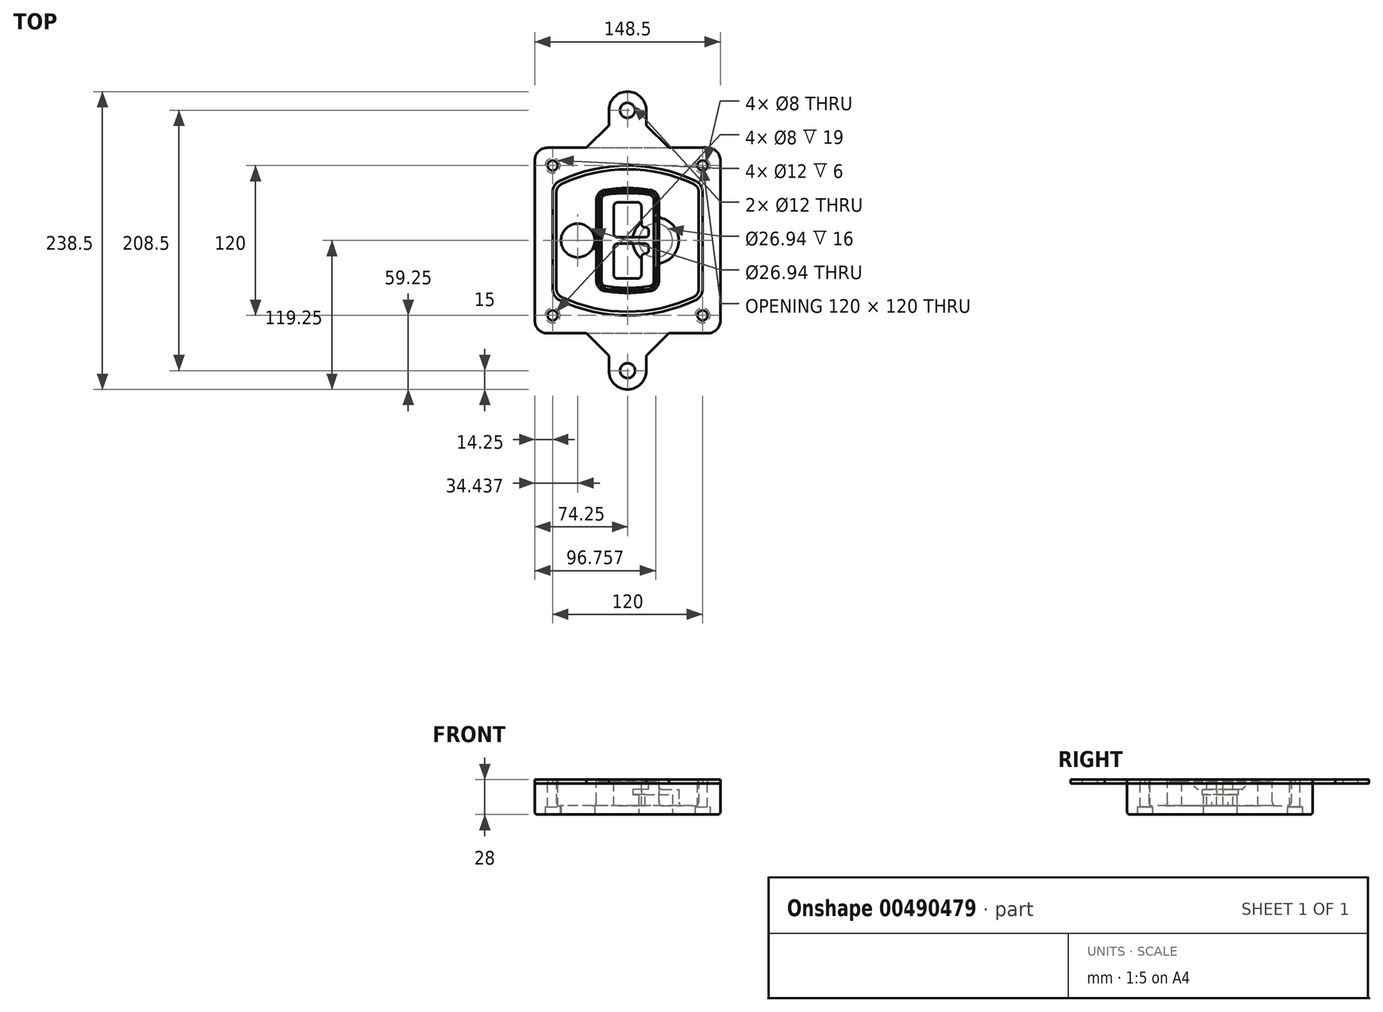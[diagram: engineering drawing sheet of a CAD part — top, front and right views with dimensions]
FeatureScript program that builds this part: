
annotation { "Feature Type Name" : "Feature", "Feature Type Description" : "" }
export const myFeature = defineFeature(function(context is Context, id is Id, definition is map)
    precondition{}
    {
        {
            var Q0;
            Q0=qCreatedBy(makeId("Top.planeOp"),FACE);
            var sketch = newSketch(context, id + "F0", { "sketchPlane" : qUnion([Q0])});
            skPoint(sketch, "E0.rect.middle", {"position": v(0, 0) * mm});
            skLineSegment(sketch, "E1.bottom", {"start": v(-64.25, -74.25) * mm, "end": v(64.25, -74.25) * mm});
            skLineSegment(sketch, "E1.top", {"start": v(-64.25, 74.25) * mm, "end": v(64.25, 74.25) * mm});
            skLineSegment(sketch, "E1.left", {"start": v(-74.25, -64.25) * mm, "end": v(-74.25, 64.25) * mm});
            skLineSegment(sketch, "E1.right", {"start": v(74.25, -64.25) * mm, "end": v(74.25, 64.25) * mm});
            skLineSegment(sketch, "E2", {"start": v(-74.25, 74.25) * mm, "end": v(74.25, -74.25) * mm, "construction": true});
            skLineSegment(sketch, "E3", {"start": v(74.25, 74.25) * mm, "end": v(-74.25, -74.25) * mm, "construction": true});
            skCircle(sketch, "E4", {"center": v(-60, 60) * mm, "radius": 4 * mm});
            skCircle(sketch, "E5", {"center": v(60, 60) * mm, "radius": 4 * mm});
            skCircle(sketch, "E6", {"center": v(60, -60) * mm, "radius": 4 * mm});
            skCircle(sketch, "E7", {"center": v(-60, -60) * mm, "radius": 4 * mm});
            skLineSegment(sketch, "E8", {"start": v(-60, 60) * mm, "end": v(60, 60) * mm, "construction": true});
            skLineSegment(sketch, "E9", {"start": v(60, 60) * mm, "end": v(60, -60) * mm, "construction": true});
            skLineSegment(sketch, "E10", {"start": v(60, -60) * mm, "end": v(-60, -60) * mm, "construction": true});
            skLineSegment(sketch, "E11", {"start": v(-60, -60) * mm, "end": v(-60, 60) * mm, "construction": true});
            skLineSegment(sketch, "E12", {"start": v(-60, 38.83) * mm, "end": v(-60, -38.83) * mm});
            skLineSegment(sketch, "E13", {"start": v(60, 38.83) * mm, "end": v(60, -38.83) * mm});
            skArc(sketch, "E14", {"start": v(54.26, 47.88) * mm, "mid": v(0, 60) * mm, "end": v(-54.26, 47.88) * mm});
            skArc(sketch, "E15", {"start": v(-54.26, -47.88) * mm, "mid": v(0, -60) * mm, "end": v(54.26, -47.88) * mm});
            skLineSegment(sketch, "E16", {"start": v(-60, 0) * mm, "end": v(60, 0) * mm, "construction": true});
            skPoint(sketch, "E17.visualSharp", {"position": v(-60, -45) * mm});
            skArc(sketch, "E17.filletArc", {"start": v(-60, -38.83) * mm, "mid": v(-58.44, -44.2) * mm, "end": v(-54.26, -47.88) * mm});
            skPoint(sketch, "E18.visualSharp", {"position": v(-60, 45) * mm});
            skArc(sketch, "E18.filletArc", {"start": v(-54.26, 47.88) * mm, "mid": v(-58.44, 44.2) * mm, "end": v(-60, 38.83) * mm});
            skPoint(sketch, "E19.visualSharp", {"position": v(60, 45) * mm});
            skArc(sketch, "E19.filletArc", {"start": v(60, 38.83) * mm, "mid": v(58.44, 44.2) * mm, "end": v(54.26, 47.88) * mm});
            skPoint(sketch, "E20.visualSharp", {"position": v(60, -45) * mm});
            skArc(sketch, "E20.filletArc", {"start": v(54.26, -47.88) * mm, "mid": v(58.44, -44.2) * mm, "end": v(60, -38.83) * mm});
            skPoint(sketch, "E21.visualSharp", {"position": v(-74.25, 74.25) * mm});
            skArc(sketch, "E21.filletArc", {"start": v(-64.25, 74.25) * mm, "mid": v(-71.32, 71.32) * mm, "end": v(-74.25, 64.25) * mm});
            skPoint(sketch, "E22.visualSharp", {"position": v(74.25, 74.25) * mm});
            skArc(sketch, "E22.filletArc", {"start": v(74.25, 64.25) * mm, "mid": v(71.32, 71.32) * mm, "end": v(64.25, 74.25) * mm});
            skPoint(sketch, "E23.visualSharp", {"position": v(74.25, -74.25) * mm});
            skArc(sketch, "E23.filletArc", {"start": v(64.25, -74.25) * mm, "mid": v(71.32, -71.32) * mm, "end": v(74.25, -64.25) * mm});
            skPoint(sketch, "E24.visualSharp", {"position": v(-74.25, -74.25) * mm});
            skArc(sketch, "E24.filletArc", {"start": v(-74.25, -64.25) * mm, "mid": v(-71.32, -71.32) * mm, "end": v(-64.25, -74.25) * mm});
            skArc(sketch, "E25.0", {"start": v(57, 38.83) * mm, "mid": v(55.9, 42.58) * mm, "end": v(52.98, 45.17) * mm});
            skLineSegment(sketch, "E25.1", {"start": v(57, 38.83) * mm, "end": v(57, -38.83) * mm});
            skArc(sketch, "E25.2", {"start": v(52.98, -45.17) * mm, "mid": v(55.9, -42.58) * mm, "end": v(57, -38.83) * mm});
            skArc(sketch, "E25.3", {"start": v(-52.98, -45.17) * mm, "mid": v(0, -57) * mm, "end": v(52.98, -45.17) * mm});
            skArc(sketch, "E25.4", {"start": v(-57, -38.83) * mm, "mid": v(-55.9, -42.58) * mm, "end": v(-52.98, -45.17) * mm});
            skArc(sketch, "E25.5", {"start": v(52.98, 45.17) * mm, "mid": v(0, 57) * mm, "end": v(-52.98, 45.17) * mm});
            skLineSegment(sketch, "E25.6", {"start": v(-57, 38.83) * mm, "end": v(-57, -38.83) * mm});
            skArc(sketch, "E25.7", {"start": v(-52.98, 45.17) * mm, "mid": v(-55.9, 42.58) * mm, "end": v(-57, 38.83) * mm});
            skArc(sketch, "E26.0", {"start": v(-55.96, 51.5) * mm, "mid": v(-61.82, 46.33) * mm, "end": v(-64, 38.83) * mm});
            skArc(sketch, "E26.1", {"start": v(55.96, 51.5) * mm, "mid": v(0, 64) * mm, "end": v(-55.96, 51.5) * mm});
            skArc(sketch, "E26.2", {"start": v(64, 38.83) * mm, "mid": v(61.82, 46.33) * mm, "end": v(55.96, 51.5) * mm});
            skLineSegment(sketch, "E26.3", {"start": v(64, 38.83) * mm, "end": v(64, -38.83) * mm});
            skArc(sketch, "E26.4", {"start": v(55.96, -51.5) * mm, "mid": v(61.82, -46.33) * mm, "end": v(64, -38.83) * mm});
            skLineSegment(sketch, "E26.5", {"start": v(-64, 38.83) * mm, "end": v(-64, -38.83) * mm});
            skArc(sketch, "E26.6", {"start": v(-55.96, -51.5) * mm, "mid": v(0, -64) * mm, "end": v(55.96, -51.5) * mm});
            skArc(sketch, "E26.7", {"start": v(-64, -38.83) * mm, "mid": v(-61.82, -46.33) * mm, "end": v(-55.96, -51.5) * mm});
            skSolve(sketch);
        }
        {
            var Q0;
            Q0=makeQuery(id+"F0.imprint","IMPRINT",FACE,{"disambiguationData":[TD([[makeQuery(id+"F0.imprint","IMPRINT",EDGE,{"derivedFrom":sQuery(id+"F0.wireOp",EDGE,"E1.bottom")}),1.0]])]});
            var Q1;
            Q1=makeQuery(id+"F0.imprint","IMPRINT",FACE,{"disambiguationData":[TD([[makeQuery(id+"F0.imprint","IMPRINT",EDGE,{"derivedFrom":sQuery(id+"F0.wireOp",EDGE,"E12")}),1.0]])]});
            var Q2;
            Q2=makeQuery(id+"F0.imprint","IMPRINT",FACE,{"disambiguationData":[TD([[makeQuery(id+"F0.imprint","IMPRINT",EDGE,{"derivedFrom":sQuery(id+"F0.wireOp",EDGE,"E25.0")}),1.0]])]});
            var Q3;
            Q3=makeQuery(id+"F0.imprint","IMPRINT",FACE,{"disambiguationData":[TD([[makeQuery(id+"F0.imprint","IMPRINT",EDGE,{"derivedFrom":sQuery(id+"F0.wireOp",EDGE,"E12")}),-1.0]])]});
            extrude(context, id + "F1", {"entities" : qUnion([Q0, Q1, Q2, Q3]), "oppositeDirection" : true, "depth" : 25 * mm});
        }
        {
            var Q0;
            Q0=makeQuery(id+"F0.imprint","IMPRINT",FACE,{"disambiguationData":[TD([[makeQuery(id+"F0.imprint","IMPRINT",EDGE,{"derivedFrom":sQuery(id+"F0.wireOp",EDGE,"E12")}),1.0]])]});
            extrude(context, id + "F2", {"entities" : qUnion([Q0]), "operationType" : NewBodyOperationType.ADD, "depth" : 3 * mm});
        }
        {
            var Q0;
            Q0=makeQuery(id+"F0.imprint","IMPRINT",FACE,{"disambiguationData":[TD([[makeQuery(id+"F0.imprint","IMPRINT",EDGE,{"derivedFrom":sQuery(id+"F0.wireOp",EDGE,"E25.0")}),1.0]])]});
            extrude(context, id + "F3", {"entities" : qUnion([Q0]), "operationType" : NewBodyOperationType.REMOVE, "oppositeDirection" : true, "depth" : 18 * mm});
        }
        {
            var Q0;
            Q0=makeQuery(id+"F2.opExtrude","CAP_FACE",FACE,{"disambiguationData":[OSD([sQuery(id+"F0.wireOp",EDGE,"E12"),sQuery(id+"F0.wireOp",EDGE,"E13"),sQuery(id+"F0.wireOp",EDGE,"E14"),sQuery(id+"F0.wireOp",EDGE,"E15"),sQuery(id+"F0.wireOp",EDGE,"E17.filletArc"),sQuery(id+"F0.wireOp",EDGE,"E18.filletArc"),sQuery(id+"F0.wireOp",EDGE,"E19.filletArc"),sQuery(id+"F0.wireOp",EDGE,"E20.filletArc"),sQuery(id+"F0.wireOp",EDGE,"E25.0"),sQuery(id+"F0.wireOp",EDGE,"E25.1"),sQuery(id+"F0.wireOp",EDGE,"E25.2"),sQuery(id+"F0.wireOp",EDGE,"E25.3"),sQuery(id+"F0.wireOp",EDGE,"E25.4"),sQuery(id+"F0.wireOp",EDGE,"E25.5"),sQuery(id+"F0.wireOp",EDGE,"E25.6"),sQuery(id+"F0.wireOp",EDGE,"E25.7")])],"isStart":false});
            var sketch = newSketch(context, id + "F4", { "sketchPlane" : qUnion([Q0])});
            skArc(sketch, "E27.0", {"start": v(-18.34, -40.45) * mm, "mid": v(0, -42) * mm, "end": v(18.34, -40.45) * mm});
            skArc(sketch, "E28.0", {"start": v(18.34, 40.45) * mm, "mid": v(0, 42) * mm, "end": v(-18.34, 40.45) * mm});
            skLineSegment(sketch, "E29", {"start": v(-25, 32.57) * mm, "end": v(-25, -32.57) * mm});
            skLineSegment(sketch, "E30", {"start": v(25, 32.57) * mm, "end": v(25, -32.57) * mm});
            skLineSegment(sketch, "E31", {"start": v(-25, 39.1) * mm, "end": v(25, 39.1) * mm, "construction": true});
            skLineSegment(sketch, "E32", {"start": v(-25, -39.1) * mm, "end": v(25, -39.1) * mm, "construction": true});
            skPoint(sketch, "E33.visualSharp", {"position": v(-25, 39.1) * mm});
            skArc(sketch, "E33.filletArc", {"start": v(-18.34, 40.45) * mm, "mid": v(-23.11, 37.73) * mm, "end": v(-25, 32.57) * mm});
            skPoint(sketch, "E34.visualSharp", {"position": v(25, 39.1) * mm});
            skArc(sketch, "E34.filletArc", {"start": v(25, 32.57) * mm, "mid": v(23.11, 37.73) * mm, "end": v(18.34, 40.45) * mm});
            skPoint(sketch, "E35.visualSharp", {"position": v(25, -39.1) * mm});
            skArc(sketch, "E35.filletArc", {"start": v(18.34, -40.45) * mm, "mid": v(23.11, -37.73) * mm, "end": v(25, -32.57) * mm});
            skPoint(sketch, "E36.visualSharp", {"position": v(-25, -39.1) * mm});
            skArc(sketch, "E36.filletArc", {"start": v(-25, -32.57) * mm, "mid": v(-23.11, -37.73) * mm, "end": v(-18.34, -40.45) * mm});
            skArc(sketch, "E37.0", {"start": v(52.98, 45.17) * mm, "mid": v(0, 57) * mm, "end": v(-52.98, 45.17) * mm});
            skArc(sketch, "E37.1", {"start": v(-52.98, 45.17) * mm, "mid": v(-55.9, 42.58) * mm, "end": v(-57, 38.83) * mm});
            skLineSegment(sketch, "E37.2", {"start": v(-57, 38.83) * mm, "end": v(-57, -38.83) * mm});
            skArc(sketch, "E37.3", {"start": v(-57, -38.83) * mm, "mid": v(-55.9, -42.58) * mm, "end": v(-52.98, -45.17) * mm});
            skArc(sketch, "E37.4", {"start": v(-52.98, -45.17) * mm, "mid": v(0, -57) * mm, "end": v(52.98, -45.17) * mm});
            skArc(sketch, "E37.5", {"start": v(52.98, -45.17) * mm, "mid": v(55.9, -42.58) * mm, "end": v(57, -38.83) * mm});
            skLineSegment(sketch, "E37.6", {"start": v(57, 38.83) * mm, "end": v(57, -38.83) * mm});
            skArc(sketch, "E37.7", {"start": v(57, 38.83) * mm, "mid": v(55.9, 42.58) * mm, "end": v(52.98, 45.17) * mm});
            skLineSegment(sketch, "E38.0", {"start": v(23, 32.57) * mm, "end": v(23, -32.57) * mm});
            skArc(sketch, "E38.1", {"start": v(18, -38.48) * mm, "mid": v(21.58, -36.44) * mm, "end": v(23, -32.57) * mm});
            skArc(sketch, "E38.2", {"start": v(-18, -38.48) * mm, "mid": v(0, -40) * mm, "end": v(18, -38.48) * mm});
            skArc(sketch, "E38.3", {"start": v(-23, -32.57) * mm, "mid": v(-21.58, -36.44) * mm, "end": v(-18, -38.48) * mm});
            skLineSegment(sketch, "E38.4", {"start": v(-23, 32.57) * mm, "end": v(-23, -32.57) * mm});
            skArc(sketch, "E38.5", {"start": v(23, 32.57) * mm, "mid": v(21.58, 36.44) * mm, "end": v(18, 38.48) * mm});
            skArc(sketch, "E38.6", {"start": v(-18, 38.48) * mm, "mid": v(-21.58, 36.44) * mm, "end": v(-23, 32.57) * mm});
            skArc(sketch, "E38.7", {"start": v(18, 38.48) * mm, "mid": v(0, 40) * mm, "end": v(-18, 38.48) * mm});
            skArc(sketch, "E39.0", {"start": v(21, 32.57) * mm, "mid": v(20.06, 35.15) * mm, "end": v(17.67, 36.5) * mm});
            skLineSegment(sketch, "E39.1", {"start": v(21, 32.57) * mm, "end": v(21, -32.57) * mm});
            skArc(sketch, "E39.2", {"start": v(17.67, -36.5) * mm, "mid": v(20.06, -35.15) * mm, "end": v(21, -32.57) * mm});
            skArc(sketch, "E39.3", {"start": v(-17.67, -36.5) * mm, "mid": v(0, -38) * mm, "end": v(17.67, -36.5) * mm});
            skArc(sketch, "E39.4", {"start": v(-21, -32.57) * mm, "mid": v(-20.06, -35.15) * mm, "end": v(-17.67, -36.5) * mm});
            skArc(sketch, "E39.5", {"start": v(17.67, 36.5) * mm, "mid": v(0, 38) * mm, "end": v(-17.67, 36.5) * mm});
            skLineSegment(sketch, "E39.6", {"start": v(-21, 32.57) * mm, "end": v(-21, -32.57) * mm});
            skArc(sketch, "E39.7", {"start": v(-17.67, 36.5) * mm, "mid": v(-20.06, 35.15) * mm, "end": v(-21, 32.57) * mm});
            skLineSegment(sketch, "E40", {"start": v(-25, 0) * mm, "end": v(25, 0) * mm, "construction": true});
            skLineSegment(sketch, "E41", {"start": v(-11, 5.5) * mm, "end": v(-11, 27.5) * mm});
            skLineSegment(sketch, "E42", {"start": v(-8, 30.5) * mm, "end": v(8, 30.5) * mm});
            skLineSegment(sketch, "E43", {"start": v(11, 27.5) * mm, "end": v(11, 13.5) * mm});
            skLineSegment(sketch, "E44", {"start": v(14, 10.5) * mm, "end": v(14, 10.5) * mm});
            skLineSegment(sketch, "E45", {"start": v(17, 7.5) * mm, "end": v(17, 5.5) * mm});
            skLineSegment(sketch, "E46", {"start": v(14, 2.5) * mm, "end": v(-8, 2.5) * mm});
            skPoint(sketch, "E47.visualSharp", {"position": v(-11, 30.5) * mm});
            skArc(sketch, "E47.filletArc", {"start": v(-8, 30.5) * mm, "mid": v(-10.12, 29.62) * mm, "end": v(-11, 27.5) * mm});
            skPoint(sketch, "E48.visualSharp", {"position": v(11, 30.5) * mm});
            skArc(sketch, "E48.filletArc", {"start": v(11, 27.5) * mm, "mid": v(10.12, 29.62) * mm, "end": v(8, 30.5) * mm});
            skPoint(sketch, "E49.visualSharp", {"position": v(11, 10.5) * mm});
            skArc(sketch, "E49.filletArc", {"start": v(11, 13.5) * mm, "mid": v(11.88, 11.38) * mm, "end": v(14, 10.5) * mm});
            skPoint(sketch, "E50.visualSharp", {"position": v(17, 10.5) * mm});
            skArc(sketch, "E50.filletArc", {"start": v(17, 7.5) * mm, "mid": v(16.12, 9.62) * mm, "end": v(14, 10.5) * mm});
            skPoint(sketch, "E51.visualSharp", {"position": v(17, 2.5) * mm});
            skArc(sketch, "E51.filletArc", {"start": v(14, 2.5) * mm, "mid": v(16.12, 3.38) * mm, "end": v(17, 5.5) * mm});
            skPoint(sketch, "E52.visualSharp", {"position": v(-11, 2.5) * mm});
            skArc(sketch, "E52.filletArc", {"start": v(-11, 5.5) * mm, "mid": v(-10.12, 3.38) * mm, "end": v(-8, 2.5) * mm});
            skLineSegment(sketch, "E53.0.MirrorCS", {"start": v(14, -2.5) * mm, "end": v(-8, -2.5) * mm});
            skArc(sketch, "E54.0.MirrorCS", {"start": v(-11, -5.5) * mm, "mid": v(-10.12, -3.38) * mm, "end": v(-8, -2.5) * mm});
            skLineSegment(sketch, "E55.0.MirrorCS", {"start": v(-11, -5.5) * mm, "end": v(-11, -27.5) * mm});
            skArc(sketch, "E56.0.MirrorCS", {"start": v(-8, -30.5) * mm, "mid": v(-10.12, -29.62) * mm, "end": v(-11, -27.5) * mm});
            skLineSegment(sketch, "E57.0.MirrorCS", {"start": v(-8, -30.5) * mm, "end": v(8, -30.5) * mm});
            skArc(sketch, "E58.0.MirrorCS", {"start": v(11, -27.5) * mm, "mid": v(10.12, -29.62) * mm, "end": v(8, -30.5) * mm});
            skLineSegment(sketch, "E59.0.MirrorCS", {"start": v(11, -27.5) * mm, "end": v(11, -13.5) * mm});
            skArc(sketch, "E60.0.MirrorCS", {"start": v(11, -13.5) * mm, "mid": v(11.88, -11.38) * mm, "end": v(14, -10.5) * mm});
            skArc(sketch, "E61.0.MirrorCS", {"start": v(17, -7.5) * mm, "mid": v(16.12, -9.62) * mm, "end": v(14, -10.5) * mm});
            skLineSegment(sketch, "E62.0.MirrorCS", {"start": v(17, -7.5) * mm, "end": v(17, -5.5) * mm});
            skArc(sketch, "E63.0.MirrorCS", {"start": v(14, -2.5) * mm, "mid": v(16.12, -3.38) * mm, "end": v(17, -5.5) * mm});
            skSolve(sketch);
        }
        {
            var Q0;
            Q0=makeQuery(id+"F4.imprint","IMPRINT",FACE,{"disambiguationData":[TD([[makeQuery(id+"F4.imprint","IMPRINT",EDGE,{"derivedFrom":sQuery(id+"F4.wireOp",EDGE,"E27.0")}),1.0]])]});
            var Q1;
            Q1=makeQuery(id+"F4.imprint","IMPRINT",FACE,{"disambiguationData":[TD([[makeQuery(id+"F4.imprint","IMPRINT",EDGE,{"derivedFrom":sQuery(id+"F4.wireOp",EDGE,"E38.0")}),-1.0]])]});
            var Q2;
            Q2=makeQuery(id+"F4.imprint","IMPRINT",FACE,{"disambiguationData":[TD([[makeQuery(id+"F4.imprint","IMPRINT",EDGE,{"derivedFrom":sQuery(id+"F4.wireOp",EDGE,"E39.0")}),1.0]])]});
            extrude(context, id + "F5", {"entities" : qUnion([Q0, Q1, Q2]), "operationType" : NewBodyOperationType.ADD, "endBound" : BoundingType.UP_TO_NEXT, "oppositeDirection" : true, "depth" : 25 * mm});
        }
        {
            var Q0;
            Q0=makeQuery(id+"F4.imprint","IMPRINT",FACE,{"disambiguationData":[TD([[makeQuery(id+"F4.imprint","IMPRINT",EDGE,{"derivedFrom":sQuery(id+"F4.wireOp",EDGE,"E38.0")}),-1.0]])]});
            extrude(context, id + "F6", {"entities" : qUnion([Q0]), "operationType" : NewBodyOperationType.REMOVE, "oppositeDirection" : true, "depth" : 2 * mm});
        }
        {
            var Q0;
            Q0=makeQuery(id+"F1.opExtrude","CAP_FACE",FACE,{"disambiguationData":[OSD([sQuery(id+"F0.wireOp",EDGE,"E1.bottom"),sQuery(id+"F0.wireOp",EDGE,"E1.top"),sQuery(id+"F0.wireOp",EDGE,"E1.left"),sQuery(id+"F0.wireOp",EDGE,"E1.right"),sQuery(id+"F0.wireOp",EDGE,"E4"),sQuery(id+"F0.wireOp",EDGE,"E5"),sQuery(id+"F0.wireOp",EDGE,"E6"),sQuery(id+"F0.wireOp",EDGE,"E7"),sQuery(id+"F0.wireOp",EDGE,"E21.filletArc"),sQuery(id+"F0.wireOp",EDGE,"E22.filletArc"),sQuery(id+"F0.wireOp",EDGE,"E23.filletArc"),sQuery(id+"F0.wireOp",EDGE,"E24.filletArc")])],"isStart":false});
            var sketch = newSketch(context, id + "F7", { "sketchPlane" : qUnion([Q0])});
            skCircle(sketch, "E64", {"center": v(22.5, 0) * mm, "radius": 13.47 * mm});
            skCircle(sketch, "E65", {"center": v(-39.81, 0) * mm, "radius": 13.47 * mm});
            skLineSegment(sketch, "E66", {"start": v(74.25, 0) * mm, "end": v(-74.25, 0) * mm});
            skCircle(sketch, "E67", {"center": v(22.5, 0) * mm, "radius": 18.47 * mm});
            skCircle(sketch, "E68", {"center": v(60, -60) * mm, "radius": 6 * mm});
            skCircle(sketch, "E69", {"center": v(-60, -60) * mm, "radius": 6 * mm});
            skCircle(sketch, "E70", {"center": v(-60, 60) * mm, "radius": 6 * mm});
            skCircle(sketch, "E71", {"center": v(60, 60) * mm, "radius": 6 * mm});
            skSolve(sketch);
        }
        {
            var Q0;
            {var subQ1=sQuery(id+"F7.wireOp",EDGE,"E66");var subQ4=sQuery(id+"F7.wireOp",EDGE,"E64");var subQ6=makeQuery(id+"F7.imprint","INTERSECT",VERTEX,{"disambiguationData":[OD(0.0)],"derivedFrom":[subQ4,subQ1]});Q0=makeQuery(id+"F7.imprint","IMPRINT",FACE,{"disambiguationData":[TD([[makeQuery(id+"F7.imprint","IMPRINT",EDGE,{"disambiguationData":[TD([[subQ6,-1.0]])],"derivedFrom":subQ4}),-1.0]])]});}
            var Q1;
            {var subQ0=sQuery(id+"F7.wireOp",EDGE,"E66");var subQ1=sQuery(id+"F7.wireOp",EDGE,"E64");var subQ3=makeQuery(id+"F7.imprint","INTERSECT",VERTEX,{"disambiguationData":[OD(0.0)],"derivedFrom":[subQ1,subQ0]});Q1=makeQuery(id+"F7.imprint","IMPRINT",FACE,{"disambiguationData":[TD([[makeQuery(id+"F7.imprint","IMPRINT",EDGE,{"disambiguationData":[TD([[subQ3,-1.0]])],"derivedFrom":subQ1}),1.0]])]});}
            var Q2;
            {var subQ0=sQuery(id+"F7.wireOp",EDGE,"E66");var subQ1=sQuery(id+"F7.wireOp",EDGE,"E64");var subQ3=makeQuery(id+"F7.imprint","INTERSECT",VERTEX,{"disambiguationData":[OD(0.0)],"derivedFrom":[subQ1,subQ0]});Q2=makeQuery(id+"F7.imprint","IMPRINT",FACE,{"disambiguationData":[TD([[makeQuery(id+"F7.imprint","IMPRINT",EDGE,{"disambiguationData":[TD([[subQ3,1.0]])],"derivedFrom":subQ1}),1.0]])]});}
            var Q3;
            {var subQ1=sQuery(id+"F7.wireOp",EDGE,"E66");var subQ4=sQuery(id+"F7.wireOp",EDGE,"E64");var subQ6=makeQuery(id+"F7.imprint","INTERSECT",VERTEX,{"disambiguationData":[OD(0.0)],"derivedFrom":[subQ4,subQ1]});Q3=makeQuery(id+"F7.imprint","IMPRINT",FACE,{"disambiguationData":[TD([[makeQuery(id+"F7.imprint","IMPRINT",EDGE,{"disambiguationData":[TD([[subQ6,1.0]])],"derivedFrom":subQ4}),-1.0]])]});}
            extrude(context, id + "F8", {"entities" : qUnion([Q0, Q1, Q2, Q3]), "operationType" : NewBodyOperationType.ADD, "oppositeDirection" : true, "depth" : 20 * mm});
        }
        {
            var Q0;
            {var subQ0=sQuery(id+"F7.wireOp",EDGE,"E66");var subQ1=sQuery(id+"F7.wireOp",EDGE,"E64");var subQ3=makeQuery(id+"F7.imprint","INTERSECT",VERTEX,{"disambiguationData":[OD(0.0)],"derivedFrom":[subQ1,subQ0]});Q0=makeQuery(id+"F7.imprint","IMPRINT",FACE,{"disambiguationData":[TD([[makeQuery(id+"F7.imprint","IMPRINT",EDGE,{"disambiguationData":[TD([[subQ3,-1.0]])],"derivedFrom":subQ1}),1.0]])]});}
            var Q1;
            {var subQ0=sQuery(id+"F7.wireOp",EDGE,"E66");var subQ1=sQuery(id+"F7.wireOp",EDGE,"E64");var subQ3=makeQuery(id+"F7.imprint","INTERSECT",VERTEX,{"disambiguationData":[OD(0.0)],"derivedFrom":[subQ1,subQ0]});Q1=makeQuery(id+"F7.imprint","IMPRINT",FACE,{"disambiguationData":[TD([[makeQuery(id+"F7.imprint","IMPRINT",EDGE,{"disambiguationData":[TD([[subQ3,1.0]])],"derivedFrom":subQ1}),1.0]])]});}
            extrude(context, id + "F9", {"entities" : qUnion([Q0, Q1]), "operationType" : NewBodyOperationType.REMOVE, "oppositeDirection" : true, "depth" : 16 * mm});
        }
        {
            var Q0;
            {var subQ0=sQuery(id+"F7.wireOp",EDGE,"E66");var subQ1=sQuery(id+"F7.wireOp",EDGE,"E65");var subQ3=makeQuery(id+"F7.imprint","INTERSECT",VERTEX,{"disambiguationData":[OD(0.0)],"derivedFrom":[subQ1,subQ0]});Q0=makeQuery(id+"F7.imprint","IMPRINT",FACE,{"disambiguationData":[TD([[makeQuery(id+"F7.imprint","IMPRINT",EDGE,{"disambiguationData":[TD([[subQ3,-1.0]])],"derivedFrom":subQ1}),1.0]])]});}
            var Q1;
            {var subQ0=sQuery(id+"F7.wireOp",EDGE,"E66");var subQ1=sQuery(id+"F7.wireOp",EDGE,"E65");var subQ3=makeQuery(id+"F7.imprint","INTERSECT",VERTEX,{"disambiguationData":[OD(0.0)],"derivedFrom":[subQ1,subQ0]});Q1=makeQuery(id+"F7.imprint","IMPRINT",FACE,{"disambiguationData":[TD([[makeQuery(id+"F7.imprint","IMPRINT",EDGE,{"disambiguationData":[TD([[subQ3,1.0]])],"derivedFrom":subQ1}),1.0]])]});}
            extrude(context, id + "F10", {"entities" : qUnion([Q0, Q1]), "operationType" : NewBodyOperationType.REMOVE, "oppositeDirection" : true, "depth" : 25 * mm});
        }
        {
            var Q0;
            Q0=makeQuery(id+"F7.imprint","IMPRINT",FACE,{"disambiguationData":[TD([[makeQuery(id+"F7.imprint","IMPRINT",EDGE,{"derivedFrom":sQuery(id+"F7.wireOp",EDGE,"E68")}),1.0]])]});
            var Q1;
            Q1=makeQuery(id+"F7.imprint","IMPRINT",FACE,{"disambiguationData":[TD([[makeQuery(id+"F7.imprint","IMPRINT",EDGE,{"derivedFrom":makeQuery(id+"F1.opExtrude","CAP_EDGE",EDGE,{"disambiguationData":[OSD([sQuery(id+"F0.wireOp",EDGE,"E5")])],"isStart":false})}),-1.0]])]});
            var Q2;
            Q2=makeQuery(id+"F7.imprint","IMPRINT",FACE,{"disambiguationData":[TD([[makeQuery(id+"F7.imprint","IMPRINT",EDGE,{"derivedFrom":sQuery(id+"F7.wireOp",EDGE,"E69")}),1.0]])]});
            var Q3;
            Q3=makeQuery(id+"F7.imprint","IMPRINT",FACE,{"disambiguationData":[TD([[makeQuery(id+"F7.imprint","IMPRINT",EDGE,{"derivedFrom":makeQuery(id+"F1.opExtrude","CAP_EDGE",EDGE,{"disambiguationData":[OSD([sQuery(id+"F0.wireOp",EDGE,"E4")])],"isStart":false})}),-1.0]])]});
            var Q4;
            Q4=makeQuery(id+"F7.imprint","IMPRINT",FACE,{"disambiguationData":[TD([[makeQuery(id+"F7.imprint","IMPRINT",EDGE,{"derivedFrom":sQuery(id+"F7.wireOp",EDGE,"E70")}),1.0]])]});
            var Q5;
            Q5=makeQuery(id+"F7.imprint","IMPRINT",FACE,{"disambiguationData":[TD([[makeQuery(id+"F7.imprint","IMPRINT",EDGE,{"derivedFrom":makeQuery(id+"F1.opExtrude","CAP_EDGE",EDGE,{"disambiguationData":[OSD([sQuery(id+"F0.wireOp",EDGE,"E7")])],"isStart":false})}),-1.0]])]});
            var Q6;
            Q6=makeQuery(id+"F7.imprint","IMPRINT",FACE,{"disambiguationData":[TD([[makeQuery(id+"F7.imprint","IMPRINT",EDGE,{"derivedFrom":sQuery(id+"F7.wireOp",EDGE,"E71")}),1.0]])]});
            var Q7;
            Q7=makeQuery(id+"F7.imprint","IMPRINT",FACE,{"disambiguationData":[TD([[makeQuery(id+"F7.imprint","IMPRINT",EDGE,{"derivedFrom":makeQuery(id+"F1.opExtrude","CAP_EDGE",EDGE,{"disambiguationData":[OSD([sQuery(id+"F0.wireOp",EDGE,"E6")])],"isStart":false})}),-1.0]])]});
            extrude(context, id + "F11", {"entities" : qUnion([Q0, Q1, Q2, Q3, Q4, Q5, Q6, Q7]), "operationType" : NewBodyOperationType.REMOVE, "oppositeDirection" : true, "depth" : 6 * mm});
        }
        {
            var Q0;
            Q0=makeQuery(id+"F9.boolean.opBoolean","COPY",FACE,{"derivedFrom":makeQuery(id+"F9.opExtrude","CAP_FACE",FACE,{"disambiguationData":[OSD([sQuery(id+"F7.wireOp",EDGE,"E64")])],"isStart":false})});
            var sketch = newSketch(context, id + "F12", { "sketchPlane" : qUnion([Q0])});
            skArc(sketch, "E72.0", {"start": v(11, 14.45) * mm, "mid": v(6.45, 9.13) * mm, "end": v(4.2, 2.5) * mm});
            skArc(sketch, "E72.1", {"start": v(4.2, -2.5) * mm, "mid": v(6.45, -9.13) * mm, "end": v(11, -14.45) * mm});
            skLineSegment(sketch, "E73", {"start": v(4.2, -2.5) * mm, "end": v(14, -2.5) * mm});
            skLineSegment(sketch, "E74.0", {"start": v(14, 2.5) * mm, "end": v(4.2, 2.5) * mm});
            skArc(sketch, "E74.1", {"start": v(14, 2.5) * mm, "mid": v(16.12, 3.38) * mm, "end": v(17, 5.5) * mm});
            skLineSegment(sketch, "E74.2", {"start": v(17, 7.5) * mm, "end": v(17, 5.5) * mm});
            skArc(sketch, "E74.3", {"start": v(17, 7.5) * mm, "mid": v(16.12, 9.62) * mm, "end": v(14, 10.5) * mm});
            skArc(sketch, "E74.4", {"start": v(11, 13.5) * mm, "mid": v(11.88, 11.38) * mm, "end": v(14, 10.5) * mm});
            skLineSegment(sketch, "E74.5", {"start": v(11, 14.45) * mm, "end": v(11, 13.5) * mm});
            skLineSegment(sketch, "E74.7", {"start": v(14, -2.5) * mm, "end": v(4.2, -2.5) * mm});
            skArc(sketch, "E74.8", {"start": v(14, -2.5) * mm, "mid": v(16.12, -3.38) * mm, "end": v(17, -5.5) * mm});
            skLineSegment(sketch, "E74.9", {"start": v(17, -7.5) * mm, "end": v(17, -5.5) * mm});
            skArc(sketch, "E74.10", {"start": v(17, -7.5) * mm, "mid": v(16.12, -9.62) * mm, "end": v(14, -10.5) * mm});
            skArc(sketch, "E74.11", {"start": v(11, -13.5) * mm, "mid": v(11.88, -11.38) * mm, "end": v(14, -10.5) * mm});
            skLineSegment(sketch, "E74.12", {"start": v(11, -14.45) * mm, "end": v(11, -13.5) * mm});
            skPoint(sketch, "E75.orphan", {"position": v(11, -27.5) * mm});
            skPoint(sketch, "E76.orphan", {"position": v(-8, -2.5) * mm});
            skPoint(sketch, "E77.orphan", {"position": v(-8, 2.5) * mm});
            skPoint(sketch, "E78.orphan", {"position": v(11, 27.5) * mm});
            skSolve(sketch);
        }
        {
            var Q0;
            {var subQ7=sQuery(id+"F12.wireOp",EDGE,"E72.0");var subQ14=sQuery(id+"F12.wireOp",EDGE,"E72.1");var subQ16=sQuery(id+"F12.wireOp",EDGE,"E74.1");var subQ18=sQuery(id+"F12.wireOp",EDGE,"E74.8");Q0=qUnion([makeQuery(id+"F12.imprint","IMPRINT",FACE,{"disambiguationData":[TD([[makeQuery(id+"F12.imprint","IMPRINT",EDGE,{"derivedFrom":subQ7}),1.0]])]}),makeQuery(id+"F12.imprint","IMPRINT",FACE,{"disambiguationData":[TD([[makeQuery(id+"F12.imprint","IMPRINT",EDGE,{"derivedFrom":subQ14}),1.0]])]}),makeQuery(id+"F12.imprint","IMPRINT",FACE,{"disambiguationData":[TD([[makeQuery(id+"F12.imprint","IMPRINT",EDGE,{"derivedFrom":subQ16}),1.0]])]}),makeQuery(id+"F12.imprint","IMPRINT",FACE,{"disambiguationData":[TD([[makeQuery(id+"F12.imprint","IMPRINT",EDGE,{"derivedFrom":subQ18}),-1.0]])]})]);}
            var Q1;
            Q1=makeQuery(id+"F5.boolean.opBoolean","SPLIT",FACE,{"disambiguationData":[TD([makeQuery(id+"F5.opExtrude","SWEPT_FACE",FACE,{"disambiguationData":[OSD([sQuery(id+"F4.wireOp",EDGE,"E41")])]})])],"derivedFrom":makeQuery(id+"F3.boolean.opBoolean","COPY",FACE,{"derivedFrom":makeQuery(id+"F3.opExtrude","CAP_FACE",FACE,{"disambiguationData":[OSD([sQuery(id+"F0.wireOp",EDGE,"E25.0"),sQuery(id+"F0.wireOp",EDGE,"E25.1"),sQuery(id+"F0.wireOp",EDGE,"E25.2"),sQuery(id+"F0.wireOp",EDGE,"E25.3"),sQuery(id+"F0.wireOp",EDGE,"E25.4"),sQuery(id+"F0.wireOp",EDGE,"E25.5"),sQuery(id+"F0.wireOp",EDGE,"E25.6"),sQuery(id+"F0.wireOp",EDGE,"E25.7")])],"isStart":false})})});
            extrude(context, id + "F13", {"entities" : qUnion([Q0]), "operationType" : NewBodyOperationType.REMOVE, "endBound" : BoundingType.UP_TO_SURFACE, "endBoundEntityFace" : qUnion([Q1]), "depth" : 25 * mm});
        }
        {
            var Q0;
            Q0=makeQuery(id+"F3.boolean.opBoolean","COPY",EDGE,{"derivedFrom":makeQuery(id+"F3.opExtrude","CAP_EDGE",EDGE,{"disambiguationData":[OSD([sQuery(id+"F0.wireOp",EDGE,"E25.6")])],"isStart":false})});
            var Q1;
            Q1=makeQuery(id+"F8.boolean.opBoolean","INTERSECT",EDGE,{"derivedFrom":[makeQuery(id+"F5.opExtrude","SWEPT_FACE",FACE,{"disambiguationData":[OSD([sQuery(id+"F4.wireOp",EDGE,"E30")])]}),makeQuery(id+"F8.opExtrude","CAP_FACE",FACE,{"disambiguationData":[OSD([sQuery(id+"F7.wireOp",EDGE,"E67")])],"isStart":false})]});
            var Q2;
            Q2=makeQuery(id+"F8.boolean.opBoolean","INTERSECT",EDGE,{"disambiguationData":[OD(1.0)],"derivedFrom":[makeQuery(id+"F5.opExtrude","SWEPT_FACE",FACE,{"disambiguationData":[OSD([sQuery(id+"F4.wireOp",EDGE,"E30")])]}),makeQuery(id+"F8.opExtrude","SWEPT_FACE",FACE,{"disambiguationData":[OSD([sQuery(id+"F7.wireOp",EDGE,"E67")])]})]});
            var Q3;
            {var subQ0=sQuery(id+"F4.wireOp",EDGE,"E30");Q3=makeQuery(id+"F8.boolean.opBoolean","SPLIT",EDGE,{"disambiguationData":[TD([makeQuery(id+"F5.opExtrude","SWEPT_FACE",FACE,{"disambiguationData":[OSD([sQuery(id+"F4.wireOp",EDGE,"E35.filletArc")])]})])],"derivedFrom":makeQuery(id+"F5.opExtrude","CAP_EDGE",EDGE,{"disambiguationData":[OSD([subQ0])],"isStart":false})});}
            var Q4;
            {var subQ0=sQuery(id+"F0.wireOp",EDGE,"E25.7");var subQ1=sQuery(id+"F0.wireOp",EDGE,"E25.1");var subQ2=sQuery(id+"F0.wireOp",EDGE,"E25.6");var subQ3=sQuery(id+"F0.wireOp",EDGE,"E25.5");var subQ4=sQuery(id+"F0.wireOp",EDGE,"E25.4");var subQ5=sQuery(id+"F0.wireOp",EDGE,"E25.0");var subQ6=sQuery(id+"F0.wireOp",EDGE,"E25.2");var subQ7=sQuery(id+"F0.wireOp",EDGE,"E25.3");Q4=makeQuery(id+"F8.boolean.opBoolean","INTERSECT",EDGE,{"derivedFrom":[makeQuery(id+"F5.boolean.opBoolean","SPLIT",FACE,{"disambiguationData":[TD([makeQuery(id+"F2.opExtrude","SWEPT_FACE",FACE,{"disambiguationData":[OSD([subQ5])]})])],"derivedFrom":makeQuery(id+"F3.boolean.opBoolean","COPY",FACE,{"derivedFrom":makeQuery(id+"F3.opExtrude","CAP_FACE",FACE,{"disambiguationData":[OSD([subQ5,subQ1,subQ6,subQ7,subQ4,subQ3,subQ2,subQ0])],"isStart":false})})}),makeQuery(id+"F8.opExtrude","SWEPT_FACE",FACE,{"disambiguationData":[OSD([sQuery(id+"F7.wireOp",EDGE,"E67")])]})]});}
            var Q5;
            Q5=makeQuery(id+"F8.boolean.opBoolean","INTERSECT",EDGE,{"disambiguationData":[OD(0.0)],"derivedFrom":[makeQuery(id+"F5.opExtrude","SWEPT_FACE",FACE,{"disambiguationData":[OSD([sQuery(id+"F4.wireOp",EDGE,"E30")])]}),makeQuery(id+"F8.opExtrude","SWEPT_FACE",FACE,{"disambiguationData":[OSD([sQuery(id+"F7.wireOp",EDGE,"E67")])]})]});
            fillet(context, id + "F14", {"entities" : qUnion([Q0, Q1, Q2, Q3, Q4, Q5]), "radius" : 3 * mm, "tangentPropagation" : true, "allowEdgeOverflow" : false});
        }
        {
            var Q0;
            Q0=makeQuery(id+"F1.opExtrude","CAP_EDGE",EDGE,{"disambiguationData":[OSD([sQuery(id+"F0.wireOp",EDGE,"E1.bottom")])],"isStart":false});
            fillet(context, id + "F15", {"entities" : qUnion([Q0]), "radius" : 2 * mm, "tangentPropagation" : true, "allowEdgeOverflow" : false});
        }
        {
            var Q0;
            {var subQ0=sQuery(id+"F0.wireOp",EDGE,"E21.filletArc");var subQ1=sQuery(id+"F0.wireOp",EDGE,"E7");var subQ2=sQuery(id+"F0.wireOp",EDGE,"E6");var subQ3=sQuery(id+"F0.wireOp",EDGE,"E5");var subQ4=sQuery(id+"F0.wireOp",EDGE,"E4");var subQ5=sQuery(id+"F0.wireOp",EDGE,"E22.filletArc");var subQ6=sQuery(id+"F0.wireOp",EDGE,"E1.bottom");var subQ7=sQuery(id+"F0.wireOp",EDGE,"E1.right");var subQ8=sQuery(id+"F0.wireOp",EDGE,"E1.top");var subQ9=sQuery(id+"F0.wireOp",EDGE,"E1.left");var subQ10=sQuery(id+"F0.wireOp",EDGE,"E23.filletArc");var subQ11=sQuery(id+"F0.wireOp",EDGE,"E24.filletArc");Q0=makeQuery(id+"F2.boolean.opBoolean","SPLIT",FACE,{"disambiguationData":[TD([makeQuery(id+"F1.opExtrude","SWEPT_FACE",FACE,{"disambiguationData":[OSD([subQ6])]})])],"derivedFrom":makeQuery(id+"F1.opExtrude","CAP_FACE",FACE,{"disambiguationData":[OSD([subQ6,subQ8,subQ9,subQ7,subQ4,subQ3,subQ2,subQ1,subQ0,subQ5,subQ10,subQ11])],"isStart":true})});}
            var sketch = newSketch(context, id + "F16", { "sketchPlane" : qUnion([Q0])});
            skLineSegment(sketch, "E79", {"start": v(0, 74.25) * mm, "end": v(0, 104.25) * mm, "construction": true});
            skArc(sketch, "E80", {"start": v(15, 104.25) * mm, "mid": v(0, 119.25) * mm, "end": v(-15, 104.25) * mm});
            skLineSegment(sketch, "E81", {"start": v(15, 104.25) * mm, "end": v(15, 92.25) * mm});
            skLineSegment(sketch, "E82", {"start": v(-15, 104.25) * mm, "end": v(-15, 92.25) * mm});
            skLineSegment(sketch, "E83", {"start": v(-15, 92.25) * mm, "end": v(-33, 74.25) * mm});
            skLineSegment(sketch, "E84", {"start": v(15, 92.25) * mm, "end": v(33, 74.25) * mm});
            skCircle(sketch, "E85", {"center": v(0, 104.25) * mm, "radius": 6 * mm});
            skLineSegment(sketch, "E86", {"start": v(-74.25, 0) * mm, "end": v(74.25, 0) * mm, "construction": true});
            skLineSegment(sketch, "E87.MirrorCS", {"start": v(15, -104.25) * mm, "end": v(15, -92.25) * mm});
            skLineSegment(sketch, "E88.MirrorCS", {"start": v(-15, -104.25) * mm, "end": v(-15, -92.25) * mm});
            skCircle(sketch, "E89.MirrorC", {"center": v(0, -104.25) * mm, "radius": 6 * mm});
            skLineSegment(sketch, "E90.MirrorCS", {"start": v(0, -74.25) * mm, "end": v(0, -104.25) * mm, "construction": true});
            skArc(sketch, "E91.MirrorCS", {"start": v(15, -104.25) * mm, "mid": v(0, -119.25) * mm, "end": v(-15, -104.25) * mm});
            skLineSegment(sketch, "E92.MirrorCS", {"start": v(-15, -92.25) * mm, "end": v(-33, -74.25) * mm});
            skLineSegment(sketch, "E93.MirrorCS", {"start": v(15, -92.25) * mm, "end": v(33, -74.25) * mm});
            skSolve(sketch);
        }
        {
            var Q0;
            Q0=makeQuery(id+"F16.imprint","IMPRINT",FACE,{"disambiguationData":[TD([[makeQuery(id+"F16.imprint","IMPRINT",EDGE,{"derivedFrom":sQuery(id+"F16.wireOp",EDGE,"E80")}),1.0]])]});
            var Q1;
            Q1=makeQuery(id+"F16.imprint","IMPRINT",FACE,{"disambiguationData":[TD([[makeQuery(id+"F16.imprint","IMPRINT",EDGE,{"derivedFrom":makeQuery(id+"F1.opExtrude","CAP_EDGE",EDGE,{"disambiguationData":[OSD([sQuery(id+"F0.wireOp",EDGE,"E1.left")])],"isStart":true})}),-1.0]])]});
            var Q2;
            Q2=makeQuery(id+"F16.imprint","IMPRINT",FACE,{"disambiguationData":[TD([[makeQuery(id+"F16.imprint","IMPRINT",EDGE,{"derivedFrom":sQuery(id+"F16.wireOp",EDGE,"E87.MirrorCS")}),1.0]])]});
            var Q3;
            Q3=makeQuery(id+"F2.opExtrude","CAP_FACE",FACE,{"disambiguationData":[OSD([sQuery(id+"F0.wireOp",EDGE,"E12"),sQuery(id+"F0.wireOp",EDGE,"E13"),sQuery(id+"F0.wireOp",EDGE,"E14"),sQuery(id+"F0.wireOp",EDGE,"E15"),sQuery(id+"F0.wireOp",EDGE,"E17.filletArc"),sQuery(id+"F0.wireOp",EDGE,"E18.filletArc"),sQuery(id+"F0.wireOp",EDGE,"E19.filletArc"),sQuery(id+"F0.wireOp",EDGE,"E20.filletArc"),sQuery(id+"F0.wireOp",EDGE,"E25.0"),sQuery(id+"F0.wireOp",EDGE,"E25.1"),sQuery(id+"F0.wireOp",EDGE,"E25.2"),sQuery(id+"F0.wireOp",EDGE,"E25.3"),sQuery(id+"F0.wireOp",EDGE,"E25.4"),sQuery(id+"F0.wireOp",EDGE,"E25.5"),sQuery(id+"F0.wireOp",EDGE,"E25.6"),sQuery(id+"F0.wireOp",EDGE,"E25.7")])],"isStart":false});
            extrude(context, id + "F17", {"entities" : qUnion([Q0, Q1, Q2]), "endBound" : BoundingType.UP_TO_SURFACE, "endBoundEntityFace" : qUnion([Q3]), "depth" : 25 * mm});
        }
    });
